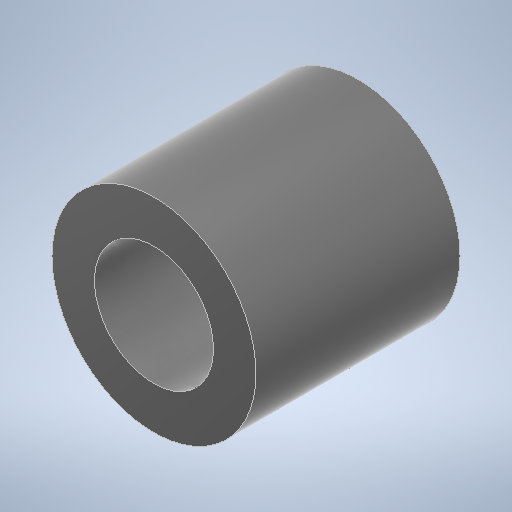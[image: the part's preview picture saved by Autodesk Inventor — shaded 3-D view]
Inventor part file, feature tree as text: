
AUTODESK INVENTOR PART (.ipt)
format: ipt  version: 2025.1 (Build 291241020, 241B)  size: 532,480 bytes
history: native  units: mm
features: extrude x1, sketch x1
ambient origin geometry x8: Origin, YZ Plane, XZ Plane, XY Plane, X Axis, Y Axis, Z Axis, Center Point
bodies: Solid1 (feature_tree)
feature tree (2):
  extrude  "Extrusion1"  Depth=6.0mm
  sketch  "Sketch1"  dims[d0=6.0mm d1=3.5mm d2=6.0mm d3=0.0mm]
